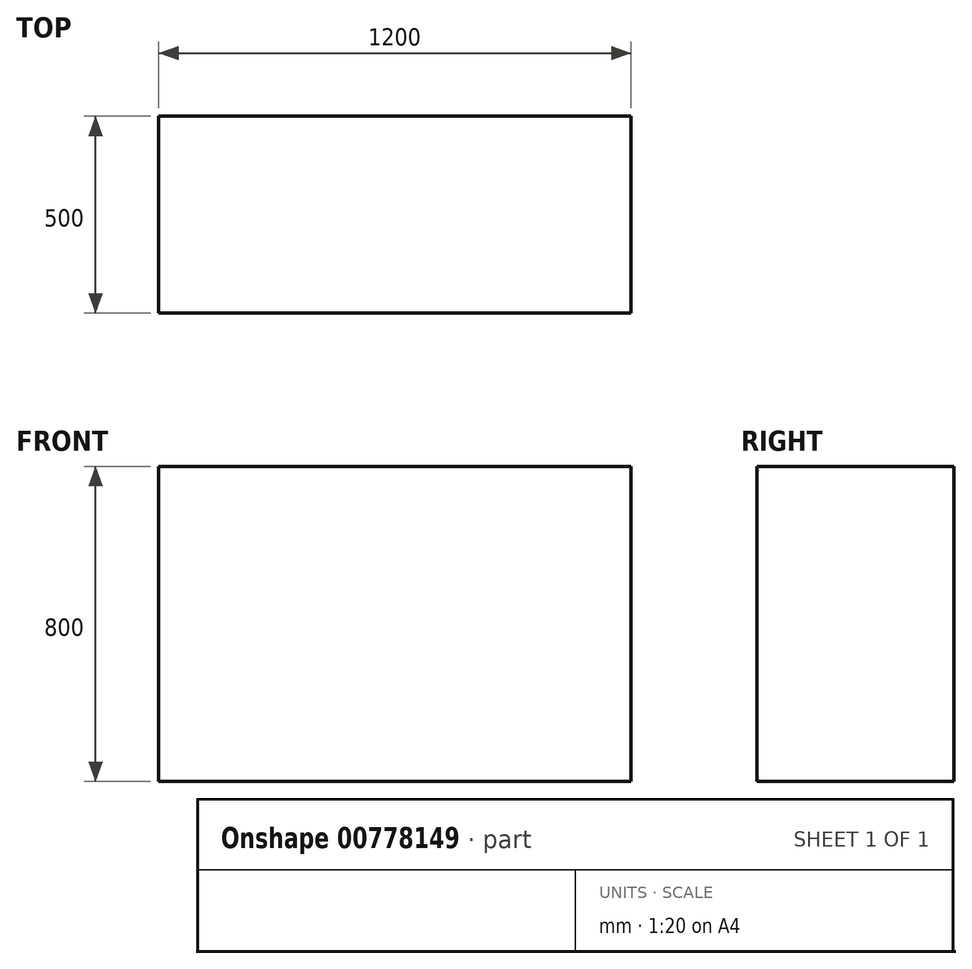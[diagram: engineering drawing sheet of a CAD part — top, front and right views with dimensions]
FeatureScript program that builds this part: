
annotation { "Feature Type Name" : "Feature", "Feature Type Description" : "" }
export const myFeature = defineFeature(function(context is Context, id is Id, definition is map)
    precondition{}
    {
        {
            var Q0;
            Q0=qCreatedBy(makeId("Top.planeOp"),FACE);
            var sketch = newSketch(context, id + "F0", { "sketchPlane" : qUnion([Q0])});
            skLineSegment(sketch, "E0.bottom", {"start": v(-600, -250) * mm, "end": v(600, -250) * mm});
            skLineSegment(sketch, "E0.top", {"start": v(-600, 250) * mm, "end": v(600, 250) * mm});
            skLineSegment(sketch, "E0.left", {"start": v(-600, -250) * mm, "end": v(-600, 250) * mm});
            skLineSegment(sketch, "E0.right", {"start": v(600, -250) * mm, "end": v(600, 250) * mm});
            skPoint(sketch, "E1", {"position": v(0, 250) * mm});
            skPoint(sketch, "E2", {"position": v(-600, 0) * mm});
            skSolve(sketch);
        }
        {
            var Q0;
            Q0=makeQuery(id+"F0.imprint","IMPRINT",FACE,{"disambiguationData":[TD([[makeQuery(id+"F0.imprint","IMPRINT",EDGE,{"derivedFrom":sQuery(id+"F0.wireOp",EDGE,"E0.bottom")}),1.0]])]});
            extrude(context, id + "F1", {"entities" : qUnion([Q0]), "depth" : 800 * mm, "offsetDistance" : 25.4 * mm});
        }
    });
